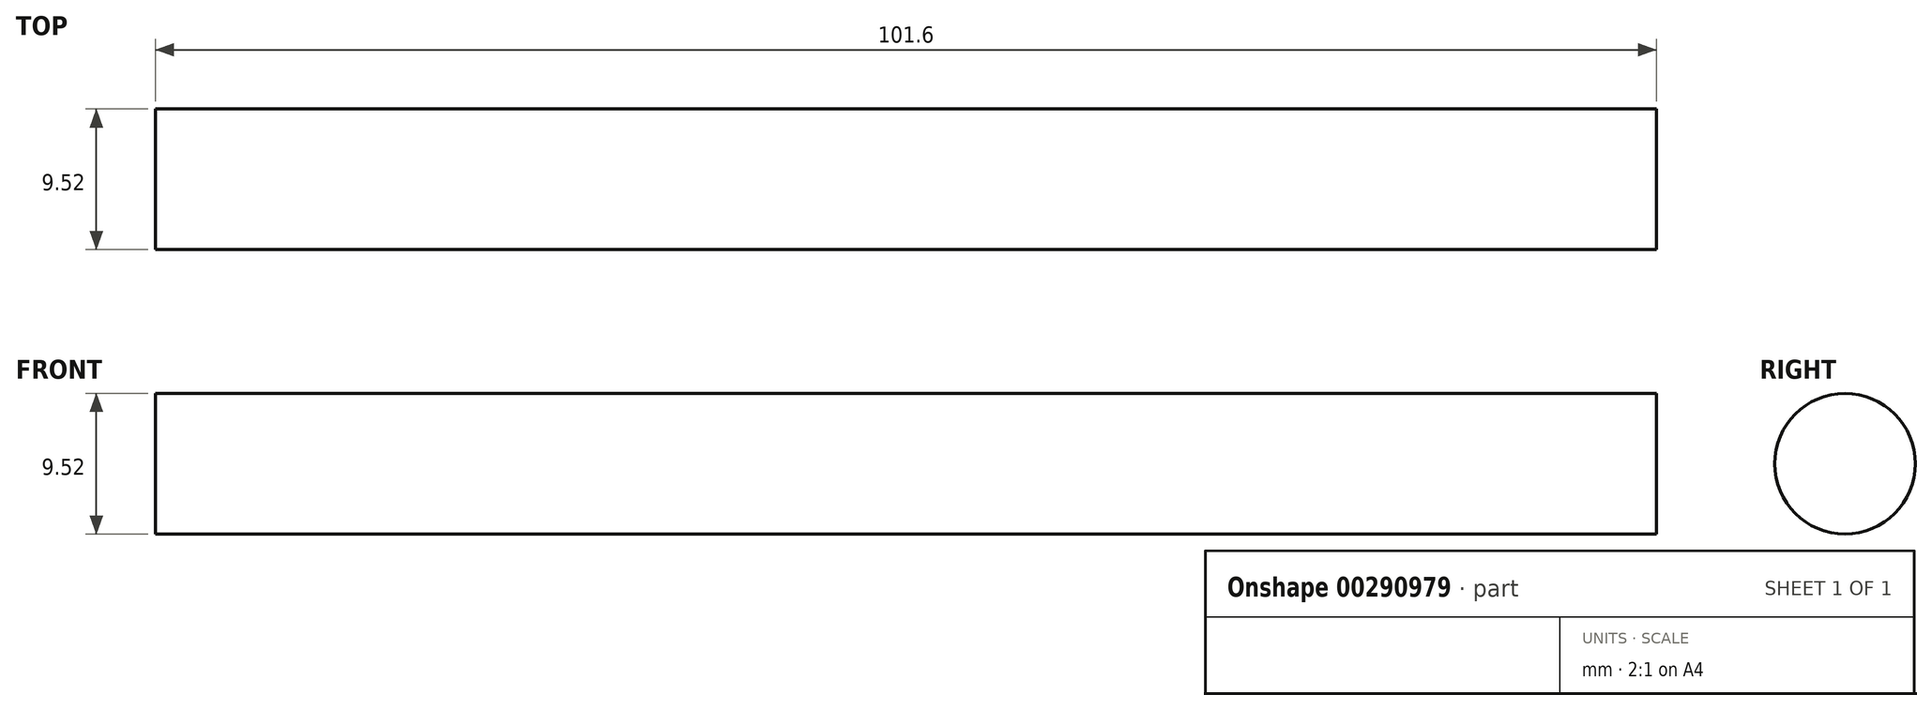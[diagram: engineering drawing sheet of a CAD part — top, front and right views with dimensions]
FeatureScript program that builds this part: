
annotation { "Feature Type Name" : "Feature", "Feature Type Description" : "" }
export const myFeature = defineFeature(function(context is Context, id is Id, definition is map)
    precondition{}
    {
        {
            var Q0;
            Q0=qCreatedBy(makeId("Right.planeOp"),FACE);
            var sketch = newSketch(context, id + "F0", { "sketchPlane" : qUnion([Q0])});
            skCircle(sketch, "E0", {"center": v(0, 0) * mm, "radius": 11.18 * mm});
            skCircle(sketch, "E1", {"center": v(0, 0) * mm, "radius": 4.76 * mm});
            skSolve(sketch);
        }
        {
            var Q0;
            Q0=makeQuery(id+"F0.imprint","IMPRINT",FACE,{"disambiguationData":[TD([[makeQuery(id+"F0.imprint","IMPRINT",EDGE,{"derivedFrom":sQuery(id+"F0.wireOp",EDGE,"E1")}),1.0]])]});
            extrude(context, id + "F1", {"entities" : qUnion([Q0]), "depth" : 101.6 * mm});
        }
    });
